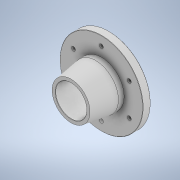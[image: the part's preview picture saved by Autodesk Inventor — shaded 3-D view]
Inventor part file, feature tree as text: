
AUTODESK INVENTOR PART (.ipt)
format: ipt  version: 2020 (Build 240168000, 168)  size: 154,624 bytes
history: native  units: in
note: dims shown in document units (in); Inventor stores cm internally (conversion verified against a paired STEP export)
features: extrude x2, chamfer x2, sketch x2
ambient origin geometry x8: Origin, YZ Plane, XZ Plane, XY Plane, X Axis, Y Axis, Z Axis, Center Point
bodies: Solid1 (feature_tree)
feature tree (6):
  extrude  "Extrusion1"  Depth=5.4764in
  extrude  "Extrusion2"  Depth=2.125in
  chamfer  "Chamfer1"  Distance=2.3622in Angle=360.0deg
  chamfer  "Chamfer2"  Distance=0.5in
  sketch  "Sketch1"  dims[d0=2.0515in d1=5.4764in]
  sketch  "Sketch2"  dims[d2=0.2656in d3=2.125in d4=2.3622in d6=360.0deg d8=0.5in d9=0.0in d10=3.0in d11=2.0in d12=0.0in d13=0.25in d14=1.625in d15=45.0deg d16=0.02in d17=1.625in d18=45.0deg]
